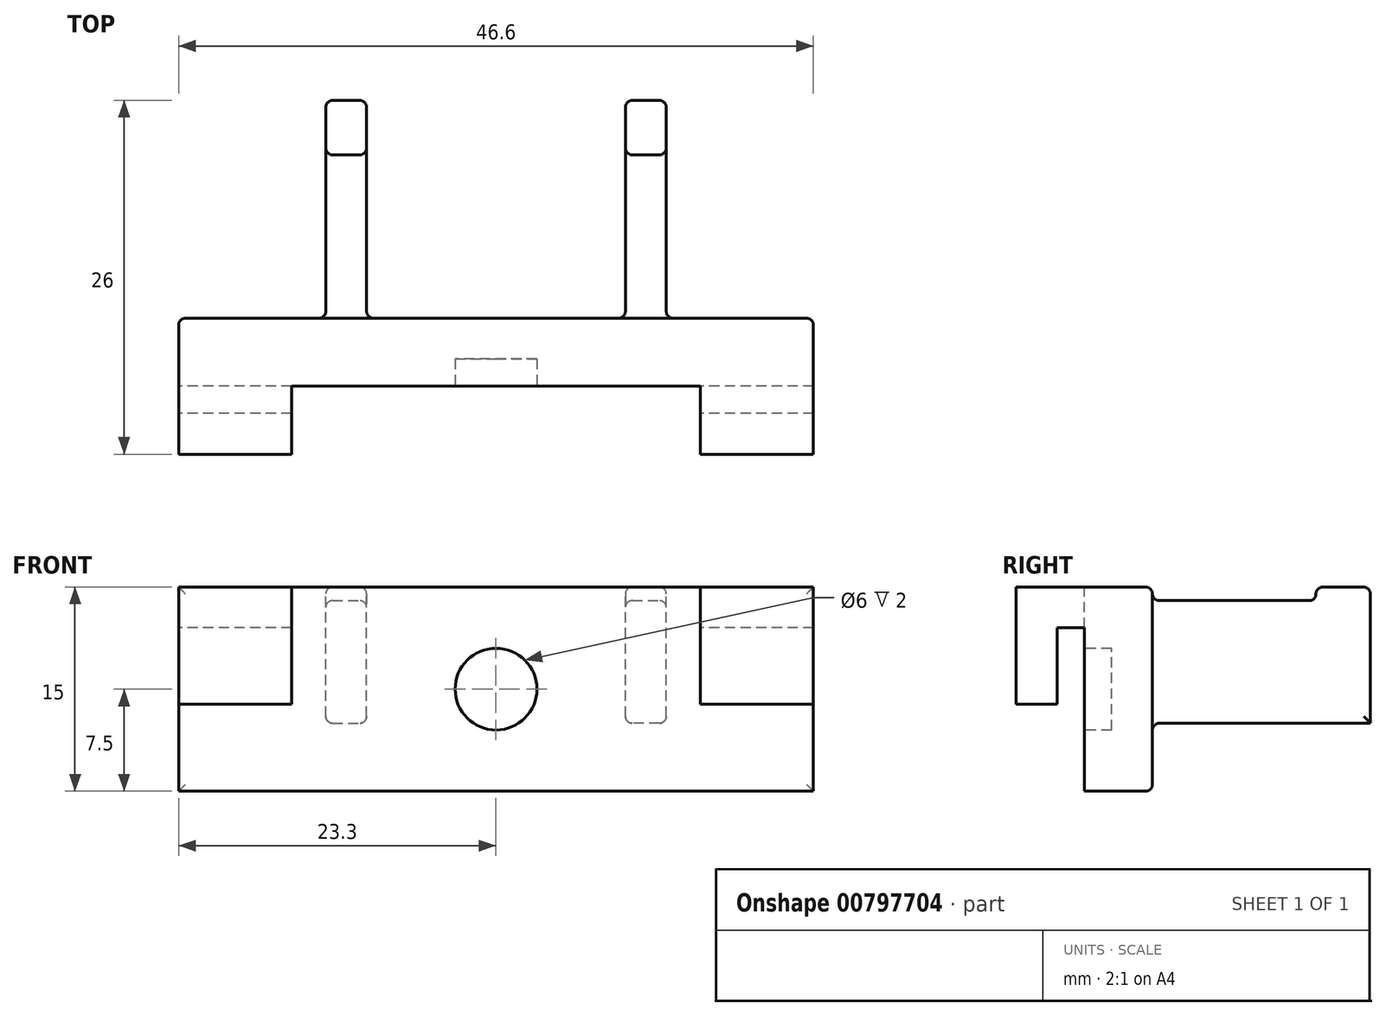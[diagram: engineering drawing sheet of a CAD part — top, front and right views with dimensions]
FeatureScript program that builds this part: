
annotation { "Feature Type Name" : "Feature", "Feature Type Description" : "" }
export const myFeature = defineFeature(function(context is Context, id is Id, definition is map)
    precondition{}
    {
        {
            var Q0;
            Q0=qCreatedBy(makeId("Right.planeOp"),FACE);
            var sketch = newSketch(context, id + "F0", { "sketchPlane" : qUnion([Q0])});
            skLineSegment(sketch, "E0", {"start": v(-5, 0) * mm, "end": v(0, 0) * mm});
            skLineSegment(sketch, "E1", {"start": v(0, 0) * mm, "end": v(0, 15) * mm});
            skLineSegment(sketch, "E2", {"start": v(0, 15) * mm, "end": v(-10, 15) * mm});
            skLineSegment(sketch, "E3", {"start": v(-10, 15) * mm, "end": v(-10, 6.4) * mm});
            skLineSegment(sketch, "E4", {"start": v(-10, 6.4) * mm, "end": v(-7, 6.4) * mm});
            skLineSegment(sketch, "E5", {"start": v(-7, 6.4) * mm, "end": v(-7, 12) * mm});
            skLineSegment(sketch, "E6", {"start": v(-7, 12) * mm, "end": v(-5, 12) * mm});
            skLineSegment(sketch, "E7", {"start": v(-5, 12) * mm, "end": v(-5, 0) * mm});
            skSolve(sketch);
        }
        {
            var Q0;
            Q0=makeQuery(id+"F0.imprint","IMPRINT",FACE,{"disambiguationData":[TD([[makeQuery(id+"F0.imprint","IMPRINT",EDGE,{"derivedFrom":sQuery(id+"F0.wireOp",EDGE,"E0")}),1.0]])]});
            extrude(context, id + "F1", {"entities" : qUnion([Q0]), "endBound" : BoundingType.SYMMETRIC, "depth" : 46.6 * mm, "offsetDistance" : 25 * mm});
        }
        {
            var Q0;
            Q0=makeQuery(id+"F1.opExtrude","SWEPT_FACE",FACE,{"disambiguationData":[OSD([sQuery(id+"F0.wireOp",EDGE,"E3")])]});
            var sketch = newSketch(context, id + "F2", { "sketchPlane" : qUnion([Q0])});
            skLineSegment(sketch, "E8.bottom", {"start": v(15, 6.4) * mm, "end": v(-15, 6.4) * mm});
            skLineSegment(sketch, "E8.top", {"start": v(15, 15) * mm, "end": v(-15, 15) * mm});
            skLineSegment(sketch, "E8.left", {"start": v(15, 6.4) * mm, "end": v(15, 15) * mm});
            skLineSegment(sketch, "E8.right", {"start": v(-15, 6.4) * mm, "end": v(-15, 15) * mm});
            skSolve(sketch);
        }
        {
            var Q0;
            Q0=makeQuery(id+"F2.imprint","IMPRINT",FACE,{"disambiguationData":[TD([[makeQuery(id+"F2.imprint","IMPRINT",EDGE,{"derivedFrom":sQuery(id+"F2.wireOp",EDGE,"E8.bottom")}),-1.0]])]});
            var Q1;
            Q1=makeQuery(id+"F1.opExtrude","SWEPT_FACE",FACE,{"disambiguationData":[OSD([sQuery(id+"F0.wireOp",EDGE,"E7")])]});
            extrude(context, id + "F3", {"entities" : qUnion([Q0]), "operationType" : NewBodyOperationType.REMOVE, "endBound" : BoundingType.UP_TO_SURFACE, "oppositeDirection" : true, "depth" : 25 * mm, "endBoundEntityFace" : qUnion([Q1]), "offsetDistance" : 25 * mm});
        }
        {
            var Q0;
            Q0=makeQuery(id+"F3.boolean.opBoolean","MERGE",FACE,{"derivedFrom":[makeQuery(id+"F1.opExtrude","SWEPT_FACE",FACE,{"disambiguationData":[OSD([sQuery(id+"F0.wireOp",EDGE,"E7")])]})],"fromTools":[makeQuery(id+"F3.opExtrude","CAP_FACE",FACE,{"disambiguationData":[OSD([sQuery(id+"F2.wireOp",EDGE,"E8.bottom"),sQuery(id+"F2.wireOp",EDGE,"E8.top"),sQuery(id+"F2.wireOp",EDGE,"E8.left"),sQuery(id+"F2.wireOp",EDGE,"E8.right")])],"isStart":false})]});
            var sketch = newSketch(context, id + "F4", { "sketchPlane" : qUnion([Q0])});
            skCircle(sketch, "E9", {"center": v(0, 7.5) * mm, "radius": 3 * mm});
            skLineSegment(sketch, "E10", {"start": v(0, 15) * mm, "end": v(0, 0) * mm, "construction": true});
            skSolve(sketch);
        }
        {
            var Q0;
            Q0=makeQuery(id+"F4.imprint","IMPRINT",FACE,{"disambiguationData":[TD([[makeQuery(id+"F4.imprint","IMPRINT",EDGE,{"derivedFrom":sQuery(id+"F4.wireOp",EDGE,"E9")}),1.0]])]});
            extrude(context, id + "F5", {"entities" : qUnion([Q0]), "operationType" : NewBodyOperationType.REMOVE, "oppositeDirection" : true, "depth" : 2 * mm, "offsetDistance" : 25 * mm});
        }
        {
            var Q0;
            Q0=makeQuery(id+"F1.opExtrude","SWEPT_FACE",FACE,{"disambiguationData":[OSD([sQuery(id+"F0.wireOp",EDGE,"E2")])]});
            var sketch = newSketch(context, id + "F6", { "sketchPlane" : qUnion([Q0])});
            skLineSegment(sketch, "E11", {"start": v(-12.5, 0) * mm, "end": v(-12.5, 16) * mm});
            skLineSegment(sketch, "E12", {"start": v(-12.5, 16) * mm, "end": v(-9.5, 16) * mm});
            skLineSegment(sketch, "E13", {"start": v(-9.5, 16) * mm, "end": v(-9.5, 13) * mm});
            skLineSegment(sketch, "E14", {"start": v(-9.5, 13) * mm, "end": v(-9.5, 13) * mm});
            skLineSegment(sketch, "E15", {"start": v(-9.5, 13) * mm, "end": v(-9.5, 0) * mm});
            skLineSegment(sketch, "E16", {"start": v(-9.5, 0) * mm, "end": v(-12.5, 0) * mm});
            skLineSegment(sketch, "E17.MirrorCS", {"start": v(9.5, 16) * mm, "end": v(9.5, 13) * mm});
            skLineSegment(sketch, "E18.MirrorCS", {"start": v(12.5, 16) * mm, "end": v(9.5, 16) * mm});
            skLineSegment(sketch, "E19.MirrorCS", {"start": v(12.5, 0) * mm, "end": v(12.5, 16) * mm});
            skLineSegment(sketch, "E20.MirrorCS", {"start": v(9.5, 13) * mm, "end": v(9.5, 0) * mm});
            skLineSegment(sketch, "E21.MirrorCS", {"start": v(9.5, 0) * mm, "end": v(12.5, 0) * mm});
            skLineSegment(sketch, "E22.MirrorCS", {"start": v(9.5, 13) * mm, "end": v(9.5, 13) * mm});
            skSolve(sketch);
        }
        {
            var Q0;
            Q0=makeQuery(id+"F6.imprint","IMPRINT",FACE,{"disambiguationData":[TD([[makeQuery(id+"F6.imprint","IMPRINT",EDGE,{"derivedFrom":sQuery(id+"F6.wireOp",EDGE,"E11")}),-1.0]])]});
            var Q1;
            Q1=makeQuery(id+"F6.imprint","IMPRINT",FACE,{"disambiguationData":[TD([[makeQuery(id+"F6.imprint","IMPRINT",EDGE,{"derivedFrom":sQuery(id+"F6.wireOp",EDGE,"E17.MirrorCS")}),1.0]])]});
            extrude(context, id + "F7", {"entities" : qUnion([Q0, Q1]), "operationType" : NewBodyOperationType.ADD, "oppositeDirection" : true, "depth" : 10 * mm, "offsetDistance" : 25 * mm});
        }
        {
            var Q0;
            Q0=makeQuery(id+"F7.opExtrude","SWEPT_FACE",FACE,{"disambiguationData":[OSD([sQuery(id+"F6.wireOp",EDGE,"E19.MirrorCS")])]});
            var sketch = newSketch(context, id + "F8", { "sketchPlane" : qUnion([Q0])});
            skLineSegment(sketch, "E23.bottom", {"start": v(0, 14) * mm, "end": v(12, 14) * mm});
            skLineSegment(sketch, "E23.top", {"start": v(0, 15) * mm, "end": v(12, 15) * mm});
            skLineSegment(sketch, "E23.left", {"start": v(0, 14) * mm, "end": v(0, 15) * mm});
            skLineSegment(sketch, "E23.right", {"start": v(12, 14) * mm, "end": v(12, 15) * mm});
            skSolve(sketch);
        }
        {
            var Q0;
            Q0=makeQuery(id+"F8.imprint","IMPRINT",FACE,{"disambiguationData":[TD([[makeQuery(id+"F8.imprint","IMPRINT",EDGE,{"derivedFrom":sQuery(id+"F8.wireOp",EDGE,"E23.bottom")}),1.0]])]});
            extrude(context, id + "F9", {"entities" : qUnion([Q0]), "operationType" : NewBodyOperationType.REMOVE, "endBound" : BoundingType.THROUGH_ALL, "oppositeDirection" : true, "depth" : 25 * mm, "offsetDistance" : 25 * mm});
        }
        {
            var Q0;
            Q0=makeQuery(id+"F7.opExtrude","SWEPT_FACE",FACE,{"disambiguationData":[OSD([sQuery(id+"F6.wireOp",EDGE,"E13"),sQuery(id+"F6.wireOp",EDGE,"E15")])]});
            var Q1;
            Q1=makeQuery(id+"F7.opExtrude","SWEPT_FACE",FACE,{"disambiguationData":[OSD([sQuery(id+"F6.wireOp",EDGE,"E19.MirrorCS")])]});
            var Q2;
            Q2=makeQuery(id+"F7.opExtrude","SWEPT_FACE",FACE,{"disambiguationData":[OSD([sQuery(id+"F6.wireOp",EDGE,"E17.MirrorCS"),sQuery(id+"F6.wireOp",EDGE,"E20.MirrorCS")])]});
            var Q3;
            Q3=makeQuery(id+"F7.opExtrude","SWEPT_FACE",FACE,{"disambiguationData":[OSD([sQuery(id+"F6.wireOp",EDGE,"E11")])]});
            var Q4;
            {var subQ0=sQuery(id+"F8.wireOp",EDGE,"E23.bottom");var subQ1=sQuery(id+"F8.wireOp",EDGE,"E23.right");Q4=makeQuery(id+"F9.boolean.opBoolean","COPY",EDGE,{"disambiguationData":[TD([makeQuery(id+"F7.opExtrude","SWEPT_FACE",FACE,{"disambiguationData":[OSD([sQuery(id+"F6.wireOp",EDGE,"E19.MirrorCS")])]})])],"derivedFrom":makeQuery(id+"F9.opExtrude","SWEPT_EDGE",EDGE,{"disambiguationData":[OSD([subQ0,subQ1])]})});}
            var Q5;
            {var subQ0=sQuery(id+"F8.wireOp",EDGE,"E23.bottom");var subQ1=sQuery(id+"F8.wireOp",EDGE,"E23.right");Q5=makeQuery(id+"F9.boolean.opBoolean","COPY",EDGE,{"disambiguationData":[TD([makeQuery(id+"F7.opExtrude","SWEPT_FACE",FACE,{"disambiguationData":[OSD([sQuery(id+"F6.wireOp",EDGE,"E11")])]})])],"derivedFrom":makeQuery(id+"F9.opExtrude","SWEPT_EDGE",EDGE,{"disambiguationData":[OSD([subQ0,subQ1])]})});}
            var Q6;
            {var subQ0=sQuery(id+"F6.wireOp",EDGE,"E11");var subQ1=sQuery(id+"F6.wireOp",EDGE,"E12");var subQ2=sQuery(id+"F6.wireOp",EDGE,"E15");var subQ3=sQuery(id+"F6.wireOp",EDGE,"E13");Q6=makeQuery(id+"F9.boolean.opBoolean","SPLIT",FACE,{"disambiguationData":[TD([makeQuery(id+"F7.opExtrude","SWEPT_FACE",FACE,{"disambiguationData":[OSD([subQ0])]})])],"derivedFrom":makeQuery(id+"F7.boolean.opBoolean","MERGE",FACE,{"derivedFrom":[makeQuery(id+"F1.opExtrude","SWEPT_FACE",FACE,{"disambiguationData":[OSD([sQuery(id+"F0.wireOp",EDGE,"E2")])]}),makeQuery(id+"F7.opExtrude","CAP_FACE",FACE,{"disambiguationData":[OSD([subQ0,subQ1,subQ3,subQ2,sQuery(id+"F6.wireOp",EDGE,"E16")])],"isStart":true}),makeQuery(id+"F7.opExtrude","CAP_FACE",FACE,{"disambiguationData":[OSD([sQuery(id+"F6.wireOp",EDGE,"E17.MirrorCS"),sQuery(id+"F6.wireOp",EDGE,"E18.MirrorCS"),sQuery(id+"F6.wireOp",EDGE,"E19.MirrorCS"),sQuery(id+"F6.wireOp",EDGE,"E20.MirrorCS"),sQuery(id+"F6.wireOp",EDGE,"E21.MirrorCS")])],"isStart":true})]})});}
            var Q7;
            {var subQ0=sQuery(id+"F6.wireOp",EDGE,"E20.MirrorCS");var subQ1=sQuery(id+"F6.wireOp",EDGE,"E17.MirrorCS");var subQ2=sQuery(id+"F6.wireOp",EDGE,"E18.MirrorCS");var subQ3=sQuery(id+"F6.wireOp",EDGE,"E19.MirrorCS");Q7=makeQuery(id+"F9.boolean.opBoolean","SPLIT",FACE,{"disambiguationData":[TD([makeQuery(id+"F7.opExtrude","SWEPT_FACE",FACE,{"disambiguationData":[OSD([subQ2])]})])],"derivedFrom":makeQuery(id+"F7.boolean.opBoolean","MERGE",FACE,{"derivedFrom":[makeQuery(id+"F1.opExtrude","SWEPT_FACE",FACE,{"disambiguationData":[OSD([sQuery(id+"F0.wireOp",EDGE,"E2")])]}),makeQuery(id+"F7.opExtrude","CAP_FACE",FACE,{"disambiguationData":[OSD([sQuery(id+"F6.wireOp",EDGE,"E11"),sQuery(id+"F6.wireOp",EDGE,"E12"),sQuery(id+"F6.wireOp",EDGE,"E13"),sQuery(id+"F6.wireOp",EDGE,"E15"),sQuery(id+"F6.wireOp",EDGE,"E16")])],"isStart":true}),makeQuery(id+"F7.opExtrude","CAP_FACE",FACE,{"disambiguationData":[OSD([subQ1,subQ2,subQ3,subQ0,sQuery(id+"F6.wireOp",EDGE,"E21.MirrorCS")])],"isStart":true})]})});}
            var Q8;
            Q8=makeQuery(id+"F9.boolean.opBoolean","MERGE",FACE,{"derivedFrom":[makeQuery(id+"F1.opExtrude","SWEPT_FACE",FACE,{"disambiguationData":[OSD([sQuery(id+"F0.wireOp",EDGE,"E1")])]}),makeQuery(id+"F9.opExtrude","SWEPT_FACE",FACE,{"disambiguationData":[OSD([sQuery(id+"F8.wireOp",EDGE,"E23.left")])]})]});
            fillet(context, id + "F10", {"entities" : qUnion([Q0, Q1, Q2, Q3, Q4, Q5, Q6, Q7, Q8]), "radius" : 0.5 * mm, "tangentPropagation" : true, "allowEdgeOverflow" : false});
        }
    });
